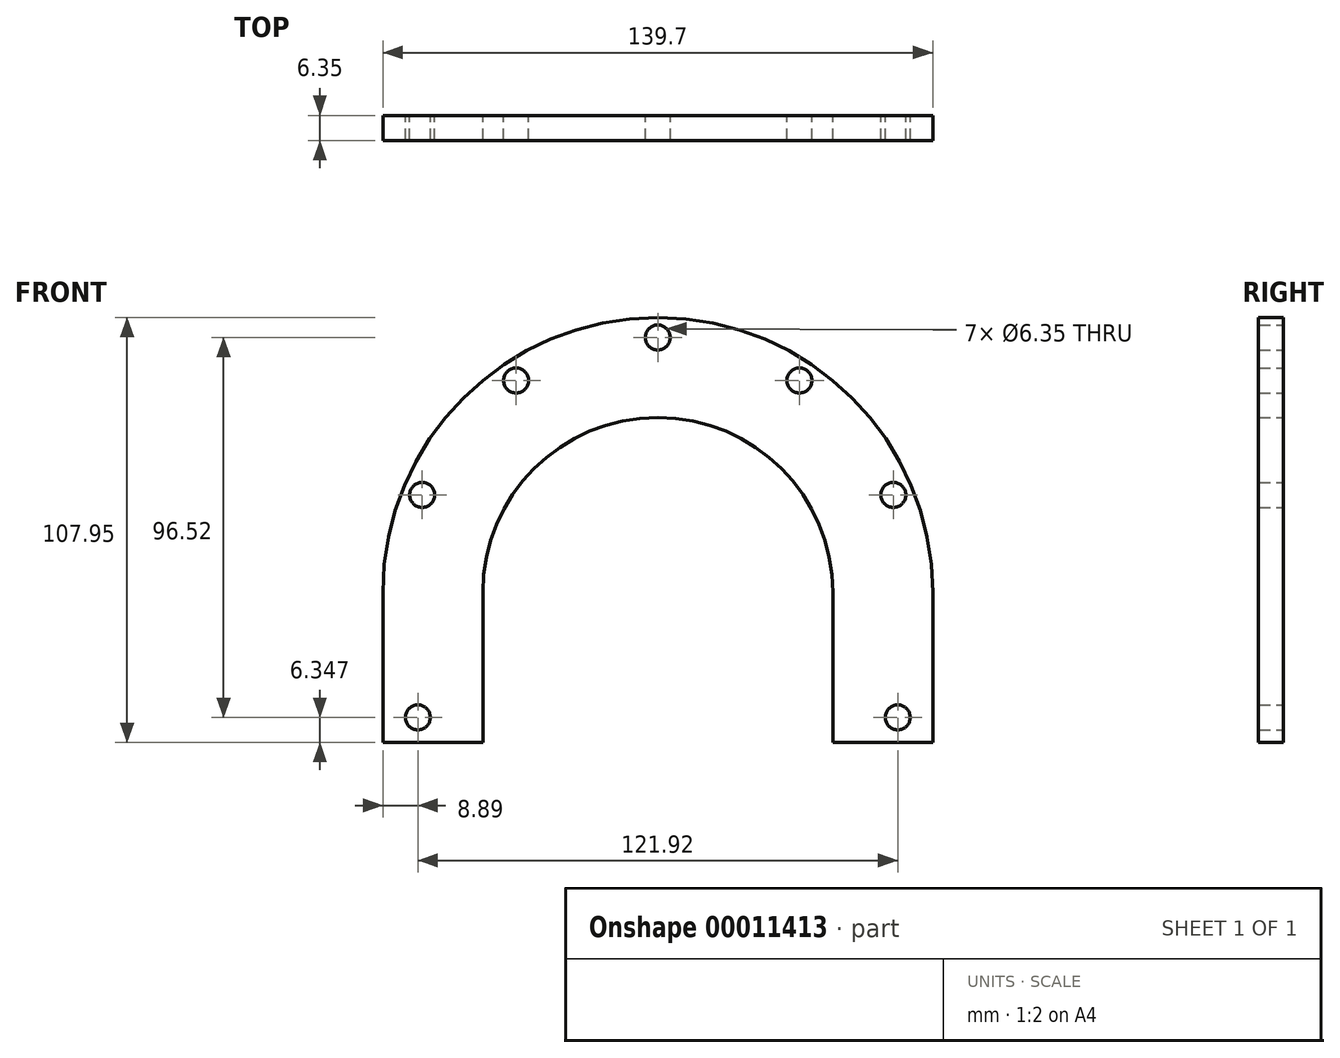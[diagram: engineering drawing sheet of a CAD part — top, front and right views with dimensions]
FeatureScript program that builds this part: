
annotation { "Feature Type Name" : "Feature", "Feature Type Description" : "" }
export const myFeature = defineFeature(function(context is Context, id is Id, definition is map)
    precondition{}
    {
        {
            var Q0;
            Q0=qCreatedBy(makeId("Front.planeOp"),FACE);
            var sketch = newSketch(context, id + "F0", { "sketchPlane" : qUnion([Q0])});
            skCircle(sketch, "E0", {"center": v(60.96, -42.45) * mm, "radius": 3.18 * mm});
            skCircle(sketch, "E1", {"center": v(0, -10.7) * mm, "radius": 60.32 * mm, "construction": true});
            skCircle(sketch, "E2", {"center": v(0, -10.7) * mm, "radius": 64.77 * mm, "construction": true});
            skArc(sketch, "E3", {"start": v(69.85, -10.7) * mm, "mid": v(0, 59.15) * mm, "end": v(-69.85, -10.7) * mm});
            skLineSegment(sketch, "E4", {"start": v(44.45, -10.7) * mm, "end": v(44.45, -48.8) * mm});
            skArc(sketch, "E5", {"start": v(44.45, -10.7) * mm, "mid": v(0, 33.75) * mm, "end": v(-44.45, -10.7) * mm});
            skLineSegment(sketch, "E6", {"start": v(69.85, -48.8) * mm, "end": v(69.85, -10.7) * mm});
            skLineSegment(sketch, "E7", {"start": v(44.45, -48.8) * mm, "end": v(69.85, -48.8) * mm});
            skLineSegment(sketch, "E8", {"start": v(-44.45, -48.8) * mm, "end": v(-69.85, -48.8) * mm});
            skLineSegment(sketch, "E9", {"start": v(-44.45, -10.7) * mm, "end": v(-44.45, -48.8) * mm});
            skCircle(sketch, "E10", {"center": v(-59.84, 14.08) * mm, "radius": 3.18 * mm});
            skLineSegment(sketch, "E11", {"start": v(-69.85, -48.8) * mm, "end": v(-69.85, -10.7) * mm});
            skCircle(sketch, "E12.2.0", {"center": v(0, 54.07) * mm, "radius": 3.18 * mm});
            skCircle(sketch, "E13", {"center": v(-60.96, -42.45) * mm, "radius": 3.18 * mm});
            skCircle(sketch, "E12.1.0", {"center": v(-35.99, 43.15) * mm, "radius": 3.18 * mm});
            skCircle(sketch, "E12.4.0", {"center": v(59.84, 14.08) * mm, "radius": 3.18 * mm});
            skLineSegment(sketch, "E12.anchor1", {"start": v(0, -10.7) * mm, "end": v(-59.84, 14.08) * mm, "construction": true});
            skCircle(sketch, "E12.3.0", {"center": v(35.98, 43.15) * mm, "radius": 3.18 * mm});
            skLineSegment(sketch, "E12.anchor2", {"start": v(0, -10.7) * mm, "end": v(59.84, 14.08) * mm, "construction": true});
            skSolve(sketch);
        }
        {
            var Q0;
            Q0 = qSketchRegion(id + "F0", true);
            extrude(context, id + "F1", {"entities" : qUnion([Q0]), "depth" : 6.35 * mm});
        }
    });
